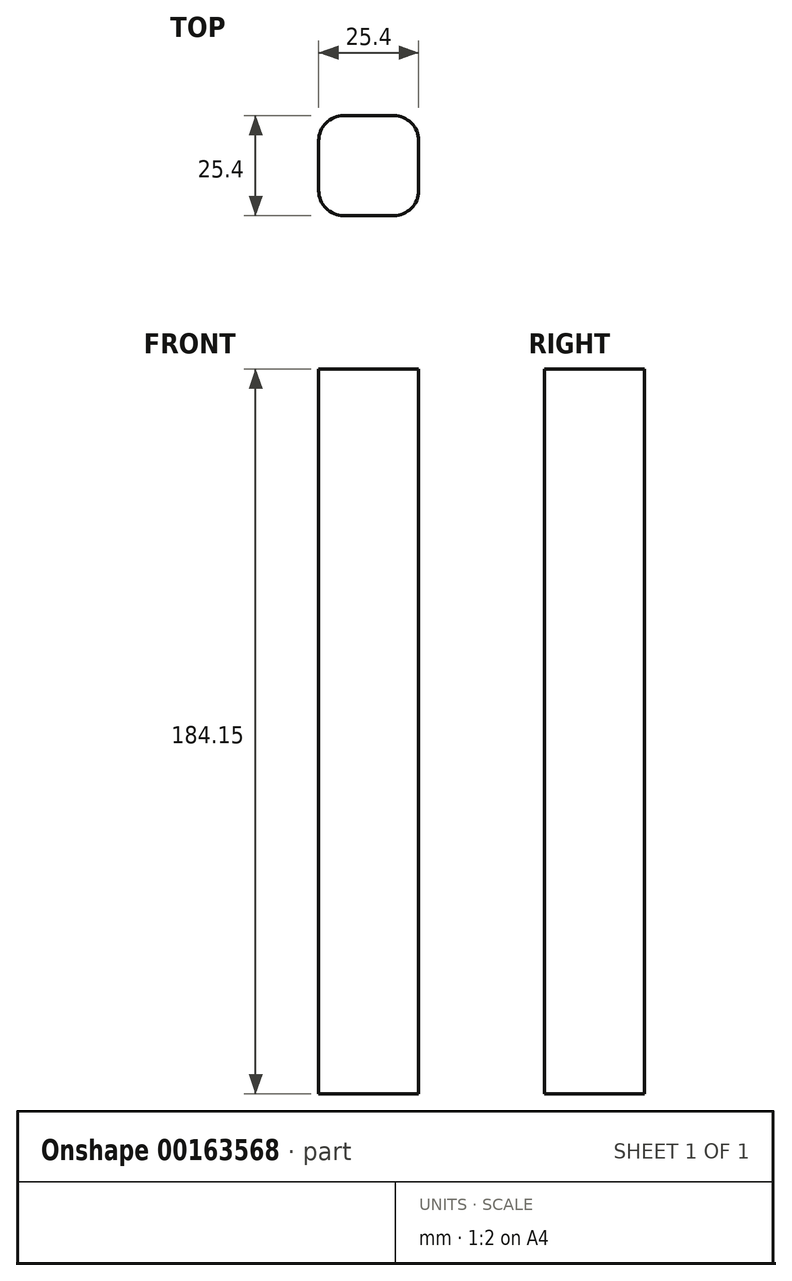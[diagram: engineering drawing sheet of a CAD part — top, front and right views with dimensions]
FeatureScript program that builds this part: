
annotation { "Feature Type Name" : "Feature", "Feature Type Description" : "" }
export const myFeature = defineFeature(function(context is Context, id is Id, definition is map)
    precondition{}
    {
        {
            var Q0;
            Q0=qCreatedBy(makeId("Top.planeOp"),FACE);
            var sketch = newSketch(context, id + "F0", { "sketchPlane" : qUnion([Q0])});
            skLineSegment(sketch, "E0.bottom", {"start": v(6.35, 12.7) * mm, "end": v(-6.35, 12.7) * mm});
            skLineSegment(sketch, "E0.top", {"start": v(6.35, -12.7) * mm, "end": v(-6.35, -12.7) * mm});
            skLineSegment(sketch, "E0.left", {"start": v(12.7, 6.35) * mm, "end": v(12.7, -6.35) * mm});
            skLineSegment(sketch, "E0.right", {"start": v(-12.7, 6.35) * mm, "end": v(-12.7, -6.35) * mm});
            skPoint(sketch, "E0.middle", {"position": v(0, 0) * mm});
            skPoint(sketch, "E1.visualSharp", {"position": v(-12.7, 12.7) * mm});
            skArc(sketch, "E1.filletArc", {"start": v(-6.35, 12.7) * mm, "mid": v(-10.84, 10.84) * mm, "end": v(-12.7, 6.35) * mm});
            skPoint(sketch, "E2.visualSharp", {"position": v(-12.7, -12.7) * mm});
            skArc(sketch, "E2.filletArc", {"start": v(-12.7, -6.35) * mm, "mid": v(-10.84, -10.84) * mm, "end": v(-6.35, -12.7) * mm});
            skPoint(sketch, "E3.visualSharp", {"position": v(12.7, -12.7) * mm});
            skArc(sketch, "E3.filletArc", {"start": v(6.35, -12.7) * mm, "mid": v(10.84, -10.84) * mm, "end": v(12.7, -6.35) * mm});
            skPoint(sketch, "E4.visualSharp", {"position": v(12.7, 12.7) * mm});
            skArc(sketch, "E4.filletArc", {"start": v(12.7, 6.35) * mm, "mid": v(10.84, 10.84) * mm, "end": v(6.35, 12.7) * mm});
            skSolve(sketch);
        }
        {
            var Q0;
            Q0=qSketchRegion(id+"F0",true);
            extrude(context, id + "F1", {"entities" : qUnion([Q0]), "depth" : 184.15 * mm, "offsetDistance" : 25.4 * mm});
        }
    });
